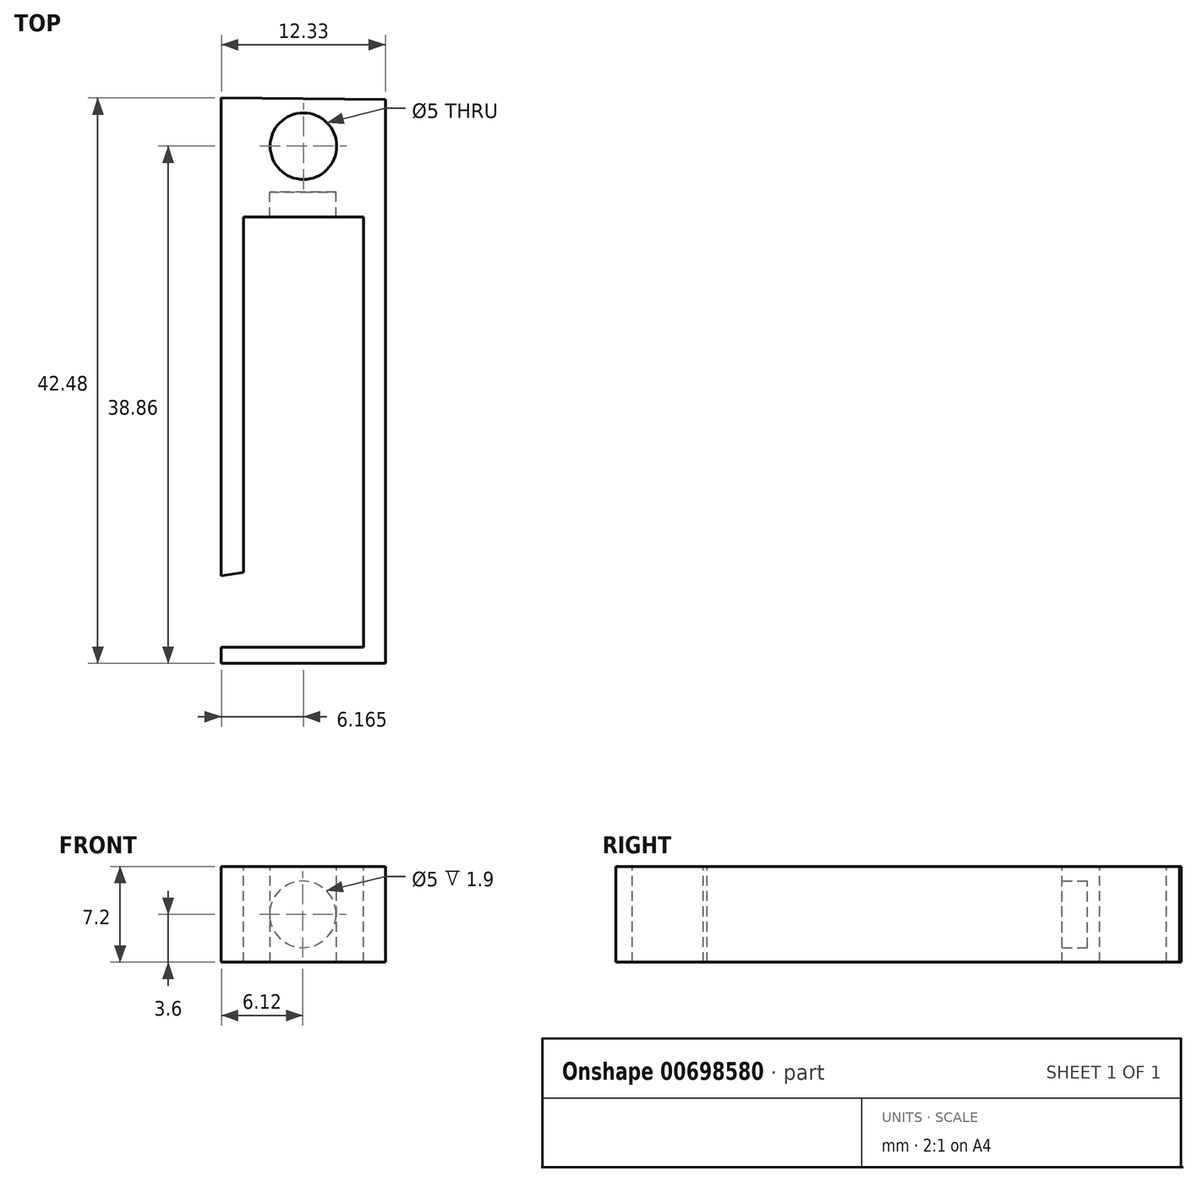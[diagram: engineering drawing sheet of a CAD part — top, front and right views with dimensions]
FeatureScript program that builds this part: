
annotation { "Feature Type Name" : "Feature", "Feature Type Description" : "" }
export const myFeature = defineFeature(function(context is Context, id is Id, definition is map)
    precondition{}
    {
        {
            var Q0;
            Q0=qCreatedBy(makeId("Top.planeOp"),FACE);
            var sketch = newSketch(context, id + "F0", { "sketchPlane" : qUnion([Q0])});
            skLineSegment(sketch, "E0", {"start": v(-23.25, 15.06) * mm, "end": v(-23.25, -13.53) * mm});
            skLineSegment(sketch, "E1", {"start": v(-23.25, 15.06) * mm, "end": v(-14.25, 15.06) * mm});
            skLineSegment(sketch, "E2", {"start": v(-14.25, 15.06) * mm, "end": v(-14.25, -19.14) * mm});
            skLineSegment(sketch, "E3", {"start": v(-23.25, -13.53) * mm, "end": v(-14.25, -19.14) * mm});
            skLineSegment(sketch, "E4", {"start": v(-14.25, -19.14) * mm, "end": v(-58.32, -19.14) * mm});
            skLineSegment(sketch, "E5", {"start": v(-58.32, -19.14) * mm, "end": v(-23.25, -13.53) * mm});
            skLineSegment(sketch, "E6", {"start": v(-24.92, -20.36) * mm, "end": v(-12.6, -20.36) * mm});
            skLineSegment(sketch, "E7", {"start": v(-12.6, -20.36) * mm, "end": v(-12.6, 22) * mm});
            skLineSegment(sketch, "E8", {"start": v(-24.92, -20.36) * mm, "end": v(-24.92, 22.12) * mm});
            skLineSegment(sketch, "E9", {"start": v(-24.92, 22.12) * mm, "end": v(-12.6, 22) * mm});
            skLineSegment(sketch, "E10", {"start": v(-23.25, -13.53) * mm, "end": v(-24.92, -13.8) * mm});
            skCircle(sketch, "E11", {"center": v(-18.75, 18.5) * mm, "radius": 2.5 * mm});
            skSolve(sketch);
        }
        {
            var Q0;
            {var subQ8=sQuery(id+"F0.wireOp",EDGE,"E0");Q0=makeQuery(id+"F0.imprint","IMPRINT",FACE,{"disambiguationData":[TD([[makeQuery(id+"F0.imprint","IMPRINT",EDGE,{"derivedFrom":subQ8}),-1.0]])]});}
            extrude(context, id + "F1", {"entities" : qUnion([Q0]), "endBound" : BoundingType.SYMMETRIC, "oppositeDirection" : true, "depth" : 7.2 * mm, "offsetDistance" : 25 * mm});
        }
        {
            var Q0;
            Q0=makeQuery(id+"F1.opExtrude","SWEPT_FACE",FACE,{"disambiguationData":[OSD([sQuery(id+"F0.wireOp",EDGE,"E1")])]});
            var sketch = newSketch(context, id + "F2", { "sketchPlane" : qUnion([Q0])});
            skCircle(sketch, "E12", {"center": v(-18.8, 0) * mm, "radius": 2.5 * mm});
            skSolve(sketch);
        }
        {
            var Q0;
            Q0=makeQuery(id+"F2.imprint","IMPRINT",FACE,{"disambiguationData":[TD([[makeQuery(id+"F2.imprint","IMPRINT",EDGE,{"derivedFrom":sQuery(id+"F2.wireOp",EDGE,"E12")}),-1.0]])]});
            extrude(context, id + "F3", {"entities" : qUnion([Q0]), "operationType" : NewBodyOperationType.ADD, "depth" : 0.8 * mm, "offsetDistance" : 25 * mm});
        }
        {
            var Q0;
            Q0=makeQuery(id+"F2.imprint","IMPRINT",FACE,{"disambiguationData":[TD([[makeQuery(id+"F2.imprint","IMPRINT",EDGE,{"derivedFrom":sQuery(id+"F2.wireOp",EDGE,"E12")}),-1.0]])]});
            extrude(context, id + "F4", {"entities" : qUnion([Q0]), "operationType" : NewBodyOperationType.ADD, "depth" : 1.9 * mm, "offsetDistance" : 25 * mm});
        }
    });
